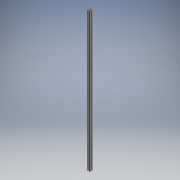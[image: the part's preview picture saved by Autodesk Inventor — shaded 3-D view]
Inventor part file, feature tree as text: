
AUTODESK INVENTOR PART (.ipt)
format: ipt  version: 2017.3 (Build 213256000, 256)  size: 210,944 bytes
history: native  units: mm (DEFAULTED — no unit token found)
features: other x21, sketch x3, hole x2, extrude x1, pattern_linear x1
ambient origin geometry x8: Origin, YZ Plane, XZ Plane, XY Plane, X Axis, Y Axis, Z Axis, Center Point
bodies: Solid1 (feature_tree)
feature tree (28):
  extrude  "Extrusion1"  Depth=1440.0mm
  hole  "Hole1"  [1 undecoded]
  hole  "Hole2"  [1 undecoded]
  pattern_linear  "Rectangular Pattern1"  [2 undecoded]
  other  "C1_XY"
  other  "C1_YZ"
  other  "C1_ZX"
  other  "C1_X"
  other  "C1_Y"
  other  "C1_Z"
  other  "C1_Center"
  other  "to_frame_cap1_XY"
  other  "to_frame_cap1_YZ"
  other  "to_frame_cap1_ZX"
  other  "to_frame_cap1_X"
  other  "to_frame_cap1_Y"
  other  "to_frame_cap1_Z"
  other  "to_frame_cap1_Center"
  other  "to_frame_cap2_XY"
  other  "to_frame_cap2_YZ"
  other  "to_frame_cap2_ZX"
  other  "to_frame_cap2_X"
  other  "to_frame_cap2_Y"
  other  "to_frame_cap2_Z"
  other  "to_frame_cap2_Center"
  sketch  "Sketch_1"  dims[d0=1440.0mm d1=0.0mm]
  sketch  "Sketch2"  dims[d2=6.8mm d3=6.0mm d4=4.0mm d5=2.0mm d6=90.0deg d7=1440.0mm d8=0.0mm]
  sketch  "Sketch3"  dims[d9=4.2mm d10=6.0mm d11=4.0mm d12=2.0mm d13=90.0deg d14=1440.0mm d15=0.0mm d16=20.0mm d18=23.2mm d19=20.0mm d21=23.2mm d22=0.0mm d23=0.0mm d24=0.0mm]
note: 4 required parameter values undecoded (feature->parameter linkage not recoverable at this tier; creation-order binding heuristic only, values carry confidence <= 0.55)
